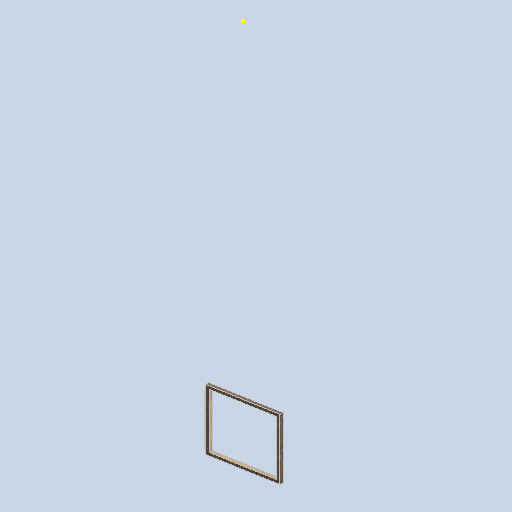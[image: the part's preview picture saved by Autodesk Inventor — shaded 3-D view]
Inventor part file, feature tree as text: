
AUTODESK INVENTOR PART (.ipt)
format: ipt  version: 2024.2 (Build 282272000, 272)  size: 324,096 bytes
history: native  units: mm
features: sketch x9, plane x4, extrude x4, loft x1, other x1, projected_geometry x1
ambient origin geometry x8: Origin, YZ Plane, XZ Plane, XY Plane, X Axis, Y Axis, Z Axis, Center Point
bodies: Solid1 (feature_tree)
feature tree (20):
  sketch  "Sketch1"  dims[d0=0.0mm d1=2500.0mm d2=150.0mm]
  plane  "Work Plane2"
  extrude  "Extrusion1"  Depth=150.0mm
  sketch  "Sketch2"  dims[d3=60.0mm d4=0.0mm d5=0.0mm]
  plane  "Work Plane3"
  sketch  "Sketch3"  dims[d6=13.962634mm d7=13.962634mm]
  plane  "Work Plane4"
  sketch  "Sketch4"  dims[d8=0.0mm d9=90.0deg d10=0.0mm d11=90.0deg]
  loft  "Loft1"
  extrude  "Extrusion2"  Depth=13.962634mm
  extrude  "Extrusion3"  TaperAngle=0.0deg  [1 undecoded]
  sketch  "Sketch8"  dims[d18=0.0mm d19=0.0mm]
  extrude  "Extrusion4"  Depth=2450.0mm
  plane  "Work Plane1"
  sketch  "Sketch5"  dims[d12=0.0mm d13=0.0mm d15=2450.0mm]
  other  "Edges1"
  sketch  "Sketch6"  dims[d16=30.0mm]
  sketch  "Sketch7"  dims[d17=2450.0mm]
  sketch  "Sketch9"  dims[d20=120.0mm d21=120.0mm d22=120.0mm d23=120.0mm d24=0.0mm d25=0.0mm]
  projected_geometry  "Projected Loop1"
note: 1 required parameter value undecoded (feature->parameter linkage not recoverable at this tier; creation-order binding heuristic only, values carry confidence <= 0.55)
